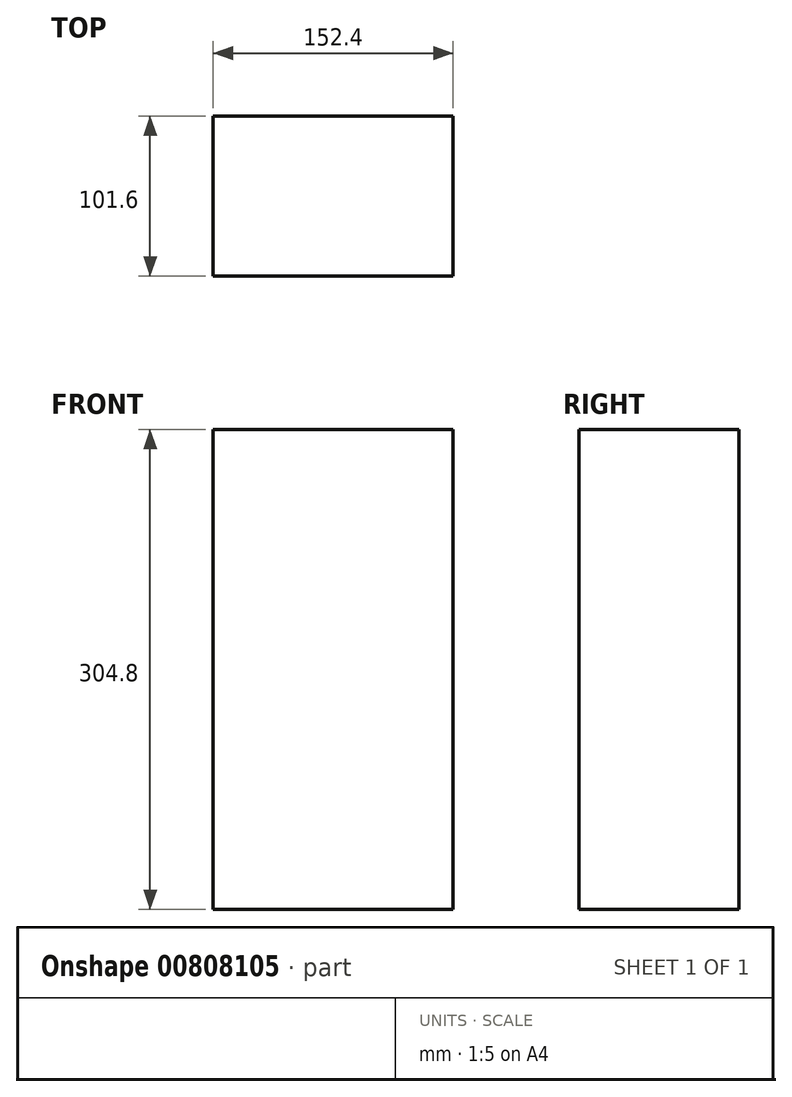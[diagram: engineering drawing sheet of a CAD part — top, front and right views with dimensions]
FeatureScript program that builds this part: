
annotation { "Feature Type Name" : "Feature", "Feature Type Description" : "" }
export const myFeature = defineFeature(function(context is Context, id is Id, definition is map)
    precondition{}
    {
        {
            var Q0;
            Q0=qCreatedBy(makeId("Front.planeOp"),FACE);
            var sketch = newSketch(context, id + "F0", { "sketchPlane" : qUnion([Q0])});
            skLineSegment(sketch, "E0.bottom", {"start": v(76.2, 152.4) * mm, "end": v(-76.2, 152.4) * mm});
            skLineSegment(sketch, "E0.top", {"start": v(76.2, -152.4) * mm, "end": v(-76.2, -152.4) * mm});
            skLineSegment(sketch, "E0.left", {"start": v(76.2, 152.4) * mm, "end": v(76.2, -152.4) * mm});
            skLineSegment(sketch, "E0.right", {"start": v(-76.2, 152.4) * mm, "end": v(-76.2, -152.4) * mm});
            skPoint(sketch, "E0.middle", {"position": v(0, 0) * mm});
            skSolve(sketch);
        }
        {
            var Q0;
            Q0=qSketchRegion(id+"F0",true);
            extrude(context, id + "F1", {"entities" : qUnion([Q0]), "depth" : 101.6 * mm, "offsetDistance" : 25.4 * mm});
        }
    });
